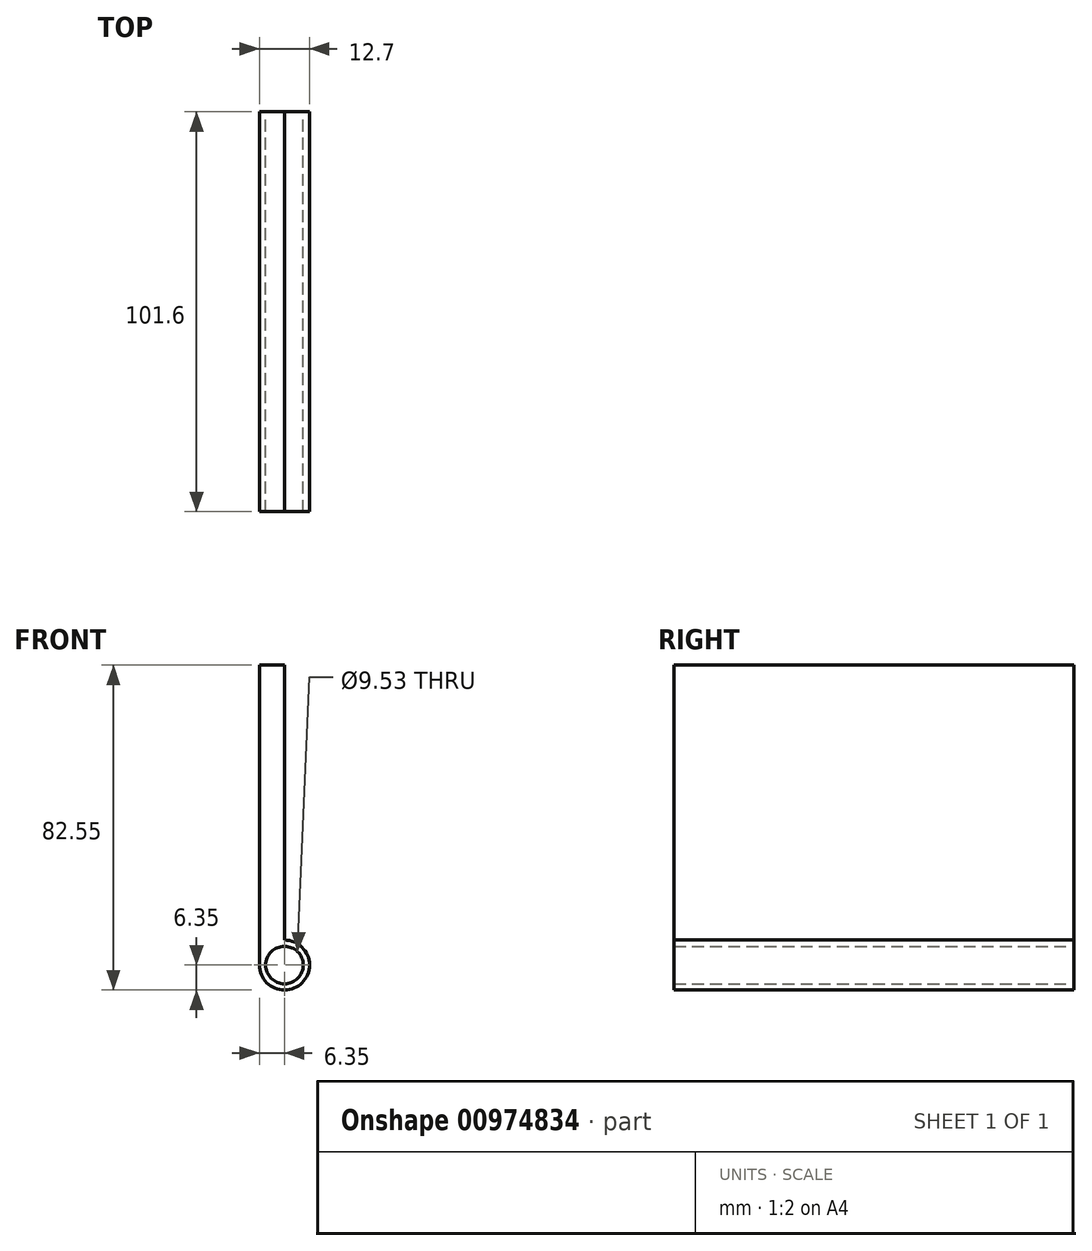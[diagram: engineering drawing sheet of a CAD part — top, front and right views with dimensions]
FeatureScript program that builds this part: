
annotation { "Feature Type Name" : "Feature", "Feature Type Description" : "" }
export const myFeature = defineFeature(function(context is Context, id is Id, definition is map)
    precondition{}
    {
        {
            var Q0;
            Q0=qCreatedBy(makeId("Front.planeOp"),FACE);
            var sketch = newSketch(context, id + "F0", { "sketchPlane" : qUnion([Q0])});
            skArc(sketch, "E0", {"start": v(-6.35, 0) * mm, "mid": v(4.5, -4.5) * mm, "end": v(0, 6.35) * mm});
            skCircle(sketch, "E1", {"center": v(0, 0) * mm, "radius": 4.76 * mm});
            skLineSegment(sketch, "E2", {"start": v(0, 6.35) * mm, "end": v(0, 76.2) * mm});
            skLineSegment(sketch, "E3", {"start": v(0, 76.2) * mm, "end": v(-6.35, 76.2) * mm});
            skLineSegment(sketch, "E4", {"start": v(-6.35, 76.2) * mm, "end": v(-6.35, 0) * mm});
            skSolve(sketch);
        }
        {
            var Q0;
            Q0 = qSketchRegion(id + "F0", true);
            extrude(context, id + "F1", {"entities" : qUnion([Q0]), "depth" : 101.6 * mm, "offsetDistance" : 25.4 * mm});
        }
    });
